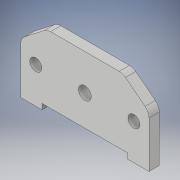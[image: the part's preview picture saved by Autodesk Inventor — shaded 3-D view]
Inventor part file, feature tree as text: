
AUTODESK INVENTOR PART (.ipt)
format: ipt  version: 2019 (Build 230136000, 136)  size: 131,072 bytes
history: native  units: mm
features: extrude x1, fillet x1, sketch x1
ambient origin geometry x8: Origin, YZ Plane, XZ Plane, XY Plane, X Axis, Y Axis, Z Axis, Center Point
bodies: Body1 (feature_tree)
feature tree (3):
  extrude  "Extrusion2"  Depth=3.2mm
  fillet  "Fillet2"  Radius=22.340214mm
  sketch  "Sketch1"  dims[d0=30.0mm d1=30.0mm d3=22.340214mm d4=75.0mm d5=7.0mm d7=7.0mm d9=28.678mm d10=28.678mm d24=7.5mm d25=6.0mm d26=0.0mm d27=6.0mm d28=50.0mm d29=12.5mm d30=3.2mm d31=37.5mm d32=22.340214mm d33=3.2mm d34=17.8mm d36=44.281401mm]
